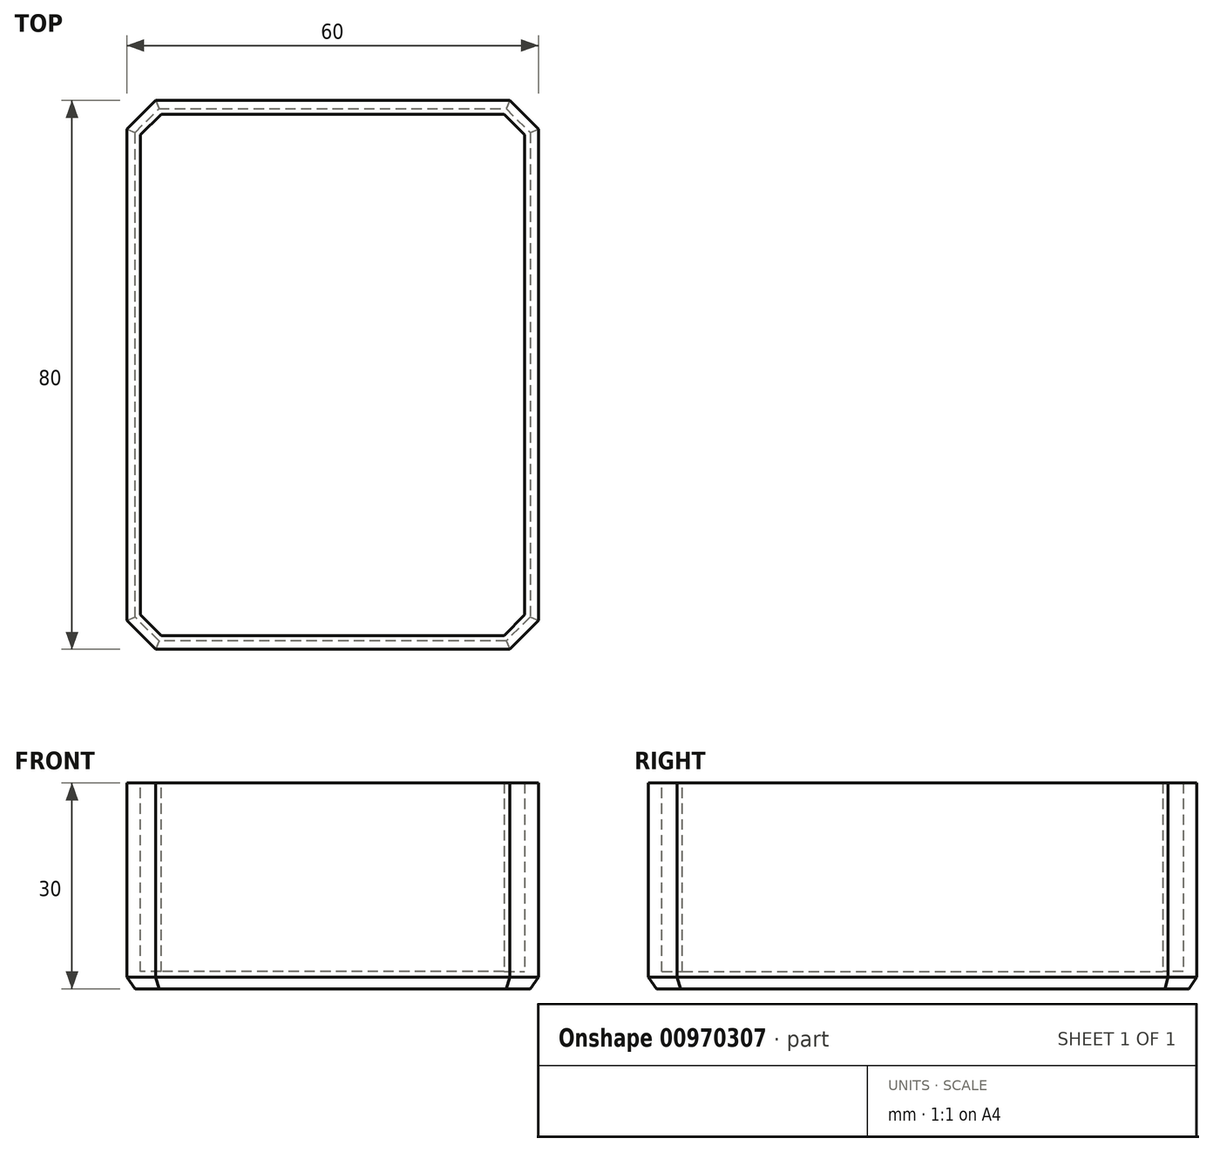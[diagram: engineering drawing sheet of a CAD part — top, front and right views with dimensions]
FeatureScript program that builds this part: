
annotation { "Feature Type Name" : "Feature", "Feature Type Description" : "" }
export const myFeature = defineFeature(function(context is Context, id is Id, definition is map)
    precondition{}
    {
        {
            var Q0;
            Q0=qCreatedBy(makeId("Top.planeOp"),FACE);
            var sketch = newSketch(context, id + "F0", { "sketchPlane" : qUnion([Q0])});
            skLineSegment(sketch, "E0.bottom", {"start": v(0, 0) * mm, "end": v(60, 0) * mm});
            skLineSegment(sketch, "E0.top", {"start": v(0, -80) * mm, "end": v(60, -80) * mm});
            skLineSegment(sketch, "E0.left", {"start": v(0, 0) * mm, "end": v(0, -80) * mm});
            skLineSegment(sketch, "E0.right", {"start": v(60, 0) * mm, "end": v(60, -80) * mm});
            skSolve(sketch);
        }
        {
            var Q0;
            Q0 = qSketchRegion(id + "F0", true);
            extrude(context, id + "F1", {"entities" : qUnion([Q0]), "depth" : 30 * mm, "offsetDistance" : 25 * mm});
        }
        {
            var Q0;
            Q0=makeQuery(id+"F1.opExtrude","CAP_FACE",FACE,{"disambiguationData":[OSD([sQuery(id+"F0.wireOp",EDGE,"E0.bottom"),sQuery(id+"F0.wireOp",EDGE,"E0.top"),sQuery(id+"F0.wireOp",EDGE,"E0.left"),sQuery(id+"F0.wireOp",EDGE,"E0.right")])],"isStart":false});
            var sketch = newSketch(context, id + "F2", { "sketchPlane" : qUnion([Q0])});
            skLineSegment(sketch, "E1.bottom", {"start": v(2, -2) * mm, "end": v(58, -2) * mm});
            skLineSegment(sketch, "E1.top", {"start": v(2, -78) * mm, "end": v(58, -78) * mm});
            skLineSegment(sketch, "E1.left", {"start": v(2, -2) * mm, "end": v(2, -78) * mm});
            skLineSegment(sketch, "E1.right", {"start": v(58, -2) * mm, "end": v(58, -78) * mm});
            skSolve(sketch);
        }
        {
            var Q0;
            Q0 = qSketchRegion(id + "F2", true);
            var Q1;
            Q1=makeQuery(id+"F1.opExtrude","CAP_FACE",FACE,{"disambiguationData":[OSD([sQuery(id+"F0.wireOp",EDGE,"E0.bottom"),sQuery(id+"F0.wireOp",EDGE,"E0.top"),sQuery(id+"F0.wireOp",EDGE,"E0.left"),sQuery(id+"F0.wireOp",EDGE,"E0.right")])],"isStart":true});
            extrude(context, id + "F3", {"entities" : qUnion([Q0]), "operationType" : NewBodyOperationType.REMOVE, "endBound" : BoundingType.UP_TO_SURFACE, "oppositeDirection" : true, "depth" : 25 * mm, "endBoundEntityFace" : qUnion([Q1]), "hasOffset" : true, "offsetDistance" : 2.5 * mm});
        }
        {
            var Q0;
            Q0=makeQuery(id+"F3.boolean.opBoolean","COPY",EDGE,{"derivedFrom":makeQuery(id+"F3.opExtrude","SWEPT_EDGE",EDGE,{"disambiguationData":[OSD([sQuery(id+"F2.wireOp",EDGE,"E1.bottom"),sQuery(id+"F2.wireOp",EDGE,"E1.right")])]})});
            var Q1;
            Q1=makeQuery(id+"F3.boolean.opBoolean","COPY",EDGE,{"derivedFrom":makeQuery(id+"F3.opExtrude","SWEPT_EDGE",EDGE,{"disambiguationData":[OSD([sQuery(id+"F2.wireOp",EDGE,"E1.bottom"),sQuery(id+"F2.wireOp",EDGE,"E1.left")])]})});
            var Q2;
            Q2=makeQuery(id+"F3.boolean.opBoolean","COPY",EDGE,{"derivedFrom":makeQuery(id+"F3.opExtrude","SWEPT_EDGE",EDGE,{"disambiguationData":[OSD([sQuery(id+"F2.wireOp",EDGE,"E1.top"),sQuery(id+"F2.wireOp",EDGE,"E1.right")])]})});
            var Q3;
            Q3=makeQuery(id+"F3.boolean.opBoolean","COPY",EDGE,{"derivedFrom":makeQuery(id+"F3.opExtrude","SWEPT_EDGE",EDGE,{"disambiguationData":[OSD([sQuery(id+"F2.wireOp",EDGE,"E1.top"),sQuery(id+"F2.wireOp",EDGE,"E1.left")])]})});
            chamfer(context, id + "F4", {"entities" : qUnion([Q0, Q1, Q2, Q3]), "width" : 3 * mm, "tangentPropagation" : true});
        }
        {
            var Q0;
            Q0=makeQuery(id+"F1.opExtrude","SWEPT_EDGE",EDGE,{"disambiguationData":[OSD([sQuery(id+"F0.wireOp",EDGE,"E0.bottom"),sQuery(id+"F0.wireOp",EDGE,"E0.left")])]});
            var Q1;
            Q1=makeQuery(id+"F1.opExtrude","SWEPT_EDGE",EDGE,{"disambiguationData":[OSD([sQuery(id+"F0.wireOp",EDGE,"E0.bottom"),sQuery(id+"F0.wireOp",EDGE,"E0.right")])]});
            var Q2;
            Q2=makeQuery(id+"F1.opExtrude","SWEPT_EDGE",EDGE,{"disambiguationData":[OSD([sQuery(id+"F0.wireOp",EDGE,"E0.top"),sQuery(id+"F0.wireOp",EDGE,"E0.right")])]});
            var Q3;
            Q3=makeQuery(id+"F1.opExtrude","SWEPT_EDGE",EDGE,{"disambiguationData":[OSD([sQuery(id+"F0.wireOp",EDGE,"E0.top"),sQuery(id+"F0.wireOp",EDGE,"E0.left")])]});
            chamfer(context, id + "F5", {"entities" : qUnion([Q0, Q1, Q2, Q3]), "width" : 4.2 * mm, "tangentPropagation" : true});
        }
        {
            var Q0;
            Q0=makeQuery(id+"F1.opExtrude","CAP_FACE",FACE,{"disambiguationData":[OSD([sQuery(id+"F0.wireOp",EDGE,"E0.bottom"),sQuery(id+"F0.wireOp",EDGE,"E0.top"),sQuery(id+"F0.wireOp",EDGE,"E0.left"),sQuery(id+"F0.wireOp",EDGE,"E0.right")])],"isStart":true});
            chamfer(context, id + "F6", {"entities" : qUnion([Q0]), "chamferType" : ChamferType.OFFSET_ANGLE, "width" : 1.2 * mm, "oppositeDirection" : false, "angle" : 55 * degree, "tangentPropagation" : true});
        }
    });
